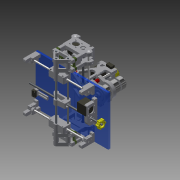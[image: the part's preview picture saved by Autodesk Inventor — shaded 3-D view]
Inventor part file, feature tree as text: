
AUTODESK INVENTOR PART (.ipt)
format: ipt  version: 2013 (Build 170138000, 138)  size: 4,507,648 bytes
history: native  units: mm
features: extrude x175, sketch x157, other x92, projected_geometry x32, fillet x19, mirror x18
ambient origin geometry x8: Origin, YZ Plane, XZ Plane, XY Plane, X Axis, Y Axis, Z Axis, Center Point
feature tree (493):
  other  "spindle.ipt"
  other  "spodnítyče"
  other  "Bloky"
  extrude  "Vysunutí1"  Depth=80.0mm
  extrude  "Vysunutí2"  Depth=4.2mm
  extrude  "Vysunutí6"  Depth=10.0mm
  extrude  "Vysunutí3"  Depth=30.0mm
  extrude  "Vysunutí4"  Depth=45.0mm
  extrude  "Vysunutí5"  Depth=300.0mm TaperAngle=0.0deg
  extrude  "Vysunutí8"  Depth=4.4mm
  extrude  "Vysunutí33"  Depth=300.0mm TaperAngle=0.0deg
  extrude  "Vysunutí9"  Depth=16.0mm
  extrude  "Vysunutí11"  Depth=100.0mm
  extrude  "Vysunutí13"  Depth=21.5mm
  extrude  "Vysunutí14"  Depth=15.0mm TaperAngle=0.0deg
  extrude  "Vysunutí15"  Depth=10.0mm TaperAngle=0.0deg
  extrude  "Vysunutí16"  Depth=15.0mm TaperAngle=0.0deg
  extrude  "Vysunutí17"  Depth=30.0mm
  extrude  "Vysunutí18"  Depth=300.0mm
  extrude  "Vysunutí20"  Depth=10.0mm
  extrude  "Vysunutí22"  Depth=250.0mm TaperAngle=0.0deg
  extrude  "Vysunutí21"  Depth=15.0mm
  extrude  "Vysunutí23"  Depth=30.0mm
  fillet  "Zaoblení1"  Radius=54.8mm
  extrude  "Vysunutí31"  Depth=110.0mm
  extrude  "Vysunutí32"  Depth=10.0mm TaperAngle=0.0deg
  extrude  "Vysunutí150"  Depth=25.0mm TaperAngle=0.0deg
  extrude  "Vysunutí44"  Depth=15.0mm TaperAngle=0.0deg
  extrude  "Vysunutí45"  Depth=80.0mm TaperAngle=0.0deg
  extrude  "Vysunutí49"  TaperAngle=0.0deg  [1 undecoded]
  extrude  "Vysunutí50"  Depth=10.0mm TaperAngle=0.0deg
  extrude  "Vysunutí51"  Depth=15.0mm TaperAngle=0.0deg
  extrude  "Vysunutí54"  Depth=15.0mm TaperAngle=0.0deg
  extrude  "Vysunutí55"  Depth=15.0mm TaperAngle=0.0deg
  extrude  "Vysunutí56"  Depth=5.0mm
  extrude  "Vysunutí57"  Depth=15.0mm TaperAngle=0.0deg
  extrude  "Vysunutí75"  Depth=15.0mm TaperAngle=0.0deg
  extrude  "Vysunutí68"  Depth=15.0mm TaperAngle=0.0deg
  extrude  "Vysunutí69"  Depth=5.0mm
  extrude  "Vysunutí65"  Depth=8.5mm
  extrude  "Vysunutí66"  Depth=11.2mm
  extrude  "Vysunutí67"  Depth=4.0mm
  fillet  "Zaoblení6"  Radius=46.0mm
  extrude  "Vysunutí71"  Depth=43.0mm
  extrude  "Vysunutí72"  Depth=37.0mm
  extrude  "Vysunutí73"  Depth=31.0mm
  extrude  "Vysunutí74"  Depth=31.0mm
  extrude  "Vysunutí76"  Depth=4.5mm
  extrude  "Vysunutí77"  Depth=80.0mm TaperAngle=0.0deg
  extrude  "Vysunutí78"  Depth=80.0mm TaperAngle=0.0deg
  sketch  "Náčrt73"
  extrude  "Vysunutí82"  Depth=7.0mm
  extrude  "Vysunutí81"  Depth=80.0mm TaperAngle=0.0deg
  extrude  "Vysunutí151"  Depth=20.0mm
  extrude  "Vysunutí228"  Depth=20.0mm
  mirror  "Zrcadlit1"
  mirror  "Zrcadlit2"
  mirror  "Zrcadlit3"
  mirror  "Zrcadlit4"
  mirror  "Zrcadlit5"
  mirror  "Zrcadlit6"
  mirror  "Zrcadlit7"
  mirror  "Zrcadlit9"
  extrude  "Vysunutí84"  Depth=5.0mm TaperAngle=0.0deg
  other  "Posunout těleso1"
  extrude  "Vysunutí85"  Depth=5.0mm TaperAngle=0.0deg
  fillet  "Zaoblení7"  Radius=15.0mm
  extrude  "Vysunutí86"  Depth=23.0mm
  extrude  "Vysunutí87"  Depth=10.0mm TaperAngle=0.0deg
  extrude  "Vysunutí88"  Depth=10.0mm TaperAngle=0.0deg
  extrude  "Vysunutí112"  Depth=23.0mm
  fillet  "Zaoblení8"  Radius=10.0mm
  mirror  "Zrcadlit10"
  mirror  "Zrcadlit11"
  mirror  "Zrcadlit12"
  extrude  "Vysunutí93"  Depth=3.0mm
  mirror  "Zrcadlit13"
  other  "Pracovní rovina26"
  extrude  "Vysunutí121"  Depth=5.0mm
  extrude  "Vysunutí136"  Depth=3.0mm
  extrude  "Vysunutí94"  Depth=3.0mm
  extrude  "Vysunutí95"  Depth=10.0mm TaperAngle=0.0deg
  extrude  "Vysunutí96"  Depth=10.0mm TaperAngle=0.0deg
  extrude  "Vysunutí97"  Depth=4.0mm
  extrude  "Vysunutí98"  Depth=10.0mm TaperAngle=0.0deg
  extrude  "Vysunutí99"  Depth=380.0mm TaperAngle=0.0deg
  extrude  "Vysunutí100"  Depth=14.0mm
  extrude  "Vysunutí101"  Depth=1.0mm
  extrude  "Vysunutí102"  Depth=10.0mm
  fillet  "Zaoblení9"  Radius=1.0mm
  fillet  "Zaoblení10"  Radius=35.0mm
  fillet  "Zaoblení11"  Radius=1.7mm
  extrude  "Vysunutí103"  Depth=14.0mm
  extrude  "Vysunutí104"  Depth=1.0mm
  other  "Pracovní rovina22"
  extrude  "Vysunutí106"  Depth=1.0mm
  other  "Pracovní rovina25"
  extrude  "Vysunutí107"  Depth=14.0mm
  extrude  "Vysunutí119"  Depth=14.0mm
  mirror  "Zrcadlit17"
  extrude  "Vysunutí124"  Depth=20.0mm
  extrude  "Vysunutí125"  Depth=3.0mm
  extrude  "Vysunutí126"  Depth=3.0mm
  extrude  "Vysunutí130"  Depth=15.0mm TaperAngle=0.0deg
  extrude  "Vysunutí127"  Depth=10.0mm TaperAngle=0.0deg
  extrude  "Vysunutí137"  Depth=10.0mm TaperAngle=0.0deg
  mirror  "Zrcadlit18"
  extrude  "Vysunutí135"  Depth=4.0mm
  other  "Kombinovat1"
  extrude  "Vysunutí143"  Depth=10.0mm TaperAngle=0.0deg
  extrude  "Vysunutí144"  Depth=10.0mm TaperAngle=0.0deg
  extrude  "Vysunutí145"  Depth=13.0mm
  extrude  "Vysunutí146"  Depth=10.0mm TaperAngle=0.0deg
  extrude  "Vysunutí147"  Depth=4.0mm
  extrude  "Vysunutí148"  Depth=6.0mm
  extrude  "Vysunutí149"  Depth=6.0mm
  extrude  "Vysunutí153"  Depth=10.0mm TaperAngle=0.0deg
  extrude  "Vysunutí154"  Depth=1.4mm
  extrude  "Vysunutí155"  Depth=1.4mm
  extrude  "Vysunutí156"  Depth=10.0mm TaperAngle=0.0deg
  extrude  "Vysunutí157"  Depth=11.2mm
  extrude  "Vysunutí158"  Depth=4.0mm TaperAngle=0.0deg
  extrude  "Vysunutí159"  Depth=15.0mm TaperAngle=0.0deg
  extrude  "Vysunutí160"  Depth=15.0mm TaperAngle=0.0deg
  extrude  "Vysunutí161"  Depth=11.2mm
  extrude  "Vysunutí162"  Depth=4.0mm TaperAngle=0.0deg
  extrude  "Vysunutí163"  Depth=0.6mm TaperAngle=0.0deg
  extrude  "Vysunutí164"  Depth=15.0mm TaperAngle=0.0deg
  extrude  "Vysunutí165"  Depth=15.0mm TaperAngle=0.0deg
  extrude  "Vysunutí166"  Depth=4.0mm
  extrude  "Vysunutí167"  Depth=300.0mm TaperAngle=0.0deg
  extrude  "Vysunutí168"  Depth=10.0mm
  extrude  "Vysunutí169"  Depth=80.0mm TaperAngle=0.0deg
  extrude  "Vysunutí170"  Depth=14.0mm
  extrude  "Vysunutí171"  Depth=15.0mm
  extrude  "Vysunutí172"  Depth=10.0mm
  extrude  "Vysunutí173"  Depth=15.0mm TaperAngle=0.0deg
  extrude  "Vysunutí174"  Depth=4.0mm
  extrude  "Vysunutí175"  Depth=1.8mm
  extrude  "Vysunutí176"  Depth=40.0mm TaperAngle=0.0deg
  extrude  "Vysunutí179"  Depth=10.0mm TaperAngle=0.0deg
  extrude  "Vysunutí180"  Depth=10.0mm TaperAngle=0.0deg
  extrude  "Vysunutí181"  Depth=2.0mm
  extrude  "Vysunutí182"  Depth=45.0mm TaperAngle=0.0deg
  extrude  "Vysunutí183"  Depth=15.0mm TaperAngle=0.0deg
  extrude  "Vysunutí184"  Depth=45.0mm
  extrude  "Vysunutí185"  Depth=10.0mm TaperAngle=0.0deg
  extrude  "Vysunutí187"  Depth=11.2mm
  extrude  "Vysunutí188"  Depth=4.0mm TaperAngle=0.0deg
  fillet  "Zaoblení12"  Radius=0.6mm
  extrude  "Vysunutí190"  Depth=30.0mm
  extrude  "Vysunutí191"  Depth=15.0mm
  extrude  "Vysunutí192"  Depth=10.0mm
  fillet  "Zaoblení13"  Radius=15.0mm
  extrude  "Vysunutí193"  Depth=10.0mm
  extrude  "Vysunutí194"  Depth=15.0mm
  extrude  "Vysunutí195"  Depth=10.0mm
  extrude  "Vysunutí196"  Depth=15.0mm
  extrude  "Vysunutí197"  Depth=15.0mm TaperAngle=0.0deg
  extrude  "Vysunutí198"  Depth=18.0mm
  extrude  "Vysunutí199"  Depth=4.0mm TaperAngle=0.0deg
  extrude  "Vysunutí200"  Depth=20.0mm
  fillet  "Zaoblení14"  Radius=20.0mm
  extrude  "Vysunutí201"  Depth=10.0mm TaperAngle=0.0deg
  extrude  "Vysunutí202"  Depth=2.5mm
  extrude  "Vysunutí203"  Depth=10.0mm TaperAngle=0.0deg
  extrude  "Vysunutí204"  Depth=20.0mm
  extrude  "Vysunutí205"  Depth=5.0mm
  fillet  "Zaoblení15"  Radius=10.0mm
  extrude  "Vysunutí206"  Depth=7.5mm
  extrude  "Vysunutí207"  Depth=10.0mm TaperAngle=0.0deg
  extrude  "Vysunutí211"  Depth=2.0mm
  extrude  "Vysunutí212"  Depth=1.0mm
  extrude  "Vysunutí213"  Depth=2.0mm TaperAngle=0.0deg
  extrude  "Vysunutí214"  Depth=5.0mm
  fillet  "Zaoblení16"  Radius=5.0mm
  extrude  "Vysunutí215"  Depth=3.0mm
  mirror  "Zrcadlit21"
  extrude  "Vysunutí216"  Depth=3.0mm
  extrude  "Vysunutí217"  Depth=3.0mm
  extrude  "Vysunutí218"  Depth=3.0mm
  fillet  "Zaoblení17"  Radius=16.0mm
  extrude  "Vysunutí220"  Depth=19.0mm
  extrude  "Vysunutí221"  Depth=5.0mm
  extrude  "Vysunutí222"  Depth=60.0mm
  extrude  "Vysunutí223"  Depth=8.1mm
  extrude  "Vysunutí224"  Depth=15.5mm
  extrude  "Vysunutí225"  Depth=50.0mm
  extrude  "Vysunutí226"  Depth=150.0mm TaperAngle=0.0deg
  extrude  "Vysunutí227"  Depth=15.3mm
  extrude  "Vysunutí229"  Depth=49.0mm TaperAngle=0.0deg
  fillet  "Zaoblení18"  Radius=15.0mm
  fillet  "Zaoblení19"  Radius=20.0mm
  extrude  "Vysunutí230"  Depth=35.0mm
  extrude  "Vysunutí231"  Depth=15.3mm
  extrude  "Vysunutí232"  Depth=24.5mm TaperAngle=0.0deg
  extrude  "Vysunutí233"  Depth=12.0mm
  extrude  "Vysunutí234"  Depth=45.0mm
  extrude  "Vysunutí235"  Depth=10.0mm
  extrude  "Vysunutí236"  Depth=15.0mm
  extrude  "Vysunutí237"  Depth=10.0mm
  extrude  "Vysunutí238"  Depth=10.0mm
  fillet  "Zaoblení20"  Radius=10.0mm
  extrude  "Vysunutí239"  Depth=10.0mm
  other  "Pracovní rovina31"
  mirror  "Zrcadlit22"
  extrude  "Vysunutí240"  Depth=10.0mm TaperAngle=0.0deg
  extrude  "Vysunutí241"  Depth=10.0mm TaperAngle=0.0deg
  extrude  "Vysunutí242"  Depth=25.0mm TaperAngle=0.0deg
  extrude  "Vysunutí243"  Depth=25.0mm TaperAngle=0.0deg
  fillet  "Zaoblení21"  Radius=25.0mm
  fillet  "Zaoblení22"  Radius=15.1mm
  mirror  "Zrcadlit23"
  mirror  "Zrcadlit24"
  other  "Závit1"
  other  "Závit2"
  other  "Závit3"
  extrude  "Vysunutí244"  Depth=25.0mm TaperAngle=0.0deg
  extrude  "Vysunutí245"  Depth=11.0mm
  extrude  "Vysunutí246"  Depth=30.0mm TaperAngle=0.0deg
  extrude  "Vysunutí247"  Depth=28.0mm
  fillet  "Zaoblení24"  Radius=30.0mm
  sketch  "Náčrt249"
  extrude  "Vysunutí248"  Depth=43.0mm
  extrude  "Vysunutí249"  Depth=47.0mm
  extrude  "Vysunutí250"  Depth=43.0mm TaperAngle=0.0deg
  sketch  "Náčrt2"
  other  "pohonY"
  sketch  "Náčrt3"
  projected_geometry  "Promítnutá smyčka1"
  projected_geometry  "Promítnutá smyčka2"
  other  "drzaky1"
  sketch  "Náčrt4"
  sketch  "Náčrt5"
  sketch  "Náčrt6"
  other  "stul"
  sketch  "Náčrt9"
  sketch  "Náčrt11"
  other  "drzaky2"
  sketch  "Náčrt14"
  other  "yvozík1"
  other  "yvozík2"
  sketch  "Náčrt18"
  projected_geometry  "Promítnutá smyčka8"
  projected_geometry  "Promítnutá smyčka9"
  sketch  "Náčrt19"
  sketch  "Náčrt20"
  sketch  "Náčrt21"
  sketch  "Náčrt23"
  sketch  "Náčrt24"
  sketch  "Náčrt25"
  sketch  "Náčrt26"
  sketch  "Náčrt27"
  sketch  "Náčrt31"
  sketch  "Náčrt33"
  sketch  "Náčrt41"
  sketch  "Náčrt44"
  sketch  "Náčrt45"
  other  "drzakxvnejsi"
  sketch  "Náčrt48"
  projected_geometry  "Promítnutá smyčka33"
  sketch  "Náčrt50"
  other  "Podložka horni"
  sketch  "Náčrt51"
  other  "posuvx"
  sketch  "Náčrt52"
  other  "tycex"
  sketch  "Náčrt53"
  sketch  "Náčrt54"
  sketch  "Náčrt56"
  sketch  "Náčrt58"
  sketch  "Náčrt60"
  other  "rozpěrka"
  sketch  "Náčrt64"
  projected_geometry  "Promítnutá smyčka40"
  sketch  "Náčrt65"
  sketch  "Náčrt67"
  other  "drzakXvnitrni"
  sketch  "Náčrt70"
  sketch  "Náčrt71"
  sketch  "Náčrt72"
  other  "Pole Podložka horni:1"
  other  "Těleso27"
  other  "Podložka"
  other  "Pole Podložka horni:2"
  other  "Těleso29"
  other  "Pole Podložka horni:3"
  other  "Těleso30"
  other  "Pole Podložka horni:4"
  other  "Těleso31"
  other  "Pole Podložka horni:5"
  other  "srzakxLnirni"
  other  "Pole Podložka horni:6"
  other  "Těleso33"
  other  "Pole Podložka horni:7"
  other  "Těleso34"
  other  "Pole Podložka horni:9"
  other  "Těleso36"
  sketch  "Náčrt77"
  other  "tyceY"
  other  "Těleso1::spindle.ipt"
  other  "Prvek štítků1"
  sketch  "Náčrt78"
  sketch  "Náčrt79"
  projected_geometry  "Promítnutá smyčka44"
  other  "NohaLZ"
  sketch  "Náčrt80"
  sketch  "Náčrt81"
  sketch  "Náčrt83"
  other  "Pole Podložka horni:10"
  other  "NohaPZ"
  other  "Pole Podložka horni:11"
  other  "NohaLP"
  other  "Pole Podložka horni:12"
  other  "NohaPP"
  sketch  "Náčrt87"
  other  "Těleso43"
  other  "Pole Podložka horni:13"
  other  "Těleso44"
  sketch  "Náčrt88"
  projected_geometry  "Promítnutá smyčka45"
  other  "drzakmotoruY"
  sketch  "Náčrt89"
  sketch  "Náčrt90"
  sketch  "Náčrt91"
  sketch  "Náčrt92"
  sketch  "Náčrt93"
  sketch  "Náčrt94"
  sketch  "Náčrt95"
  sketch  "Náčrt96"
  sketch  "Náčrt97"
  sketch  "Náčrt98"
  other  "vozikxstřed"
  sketch  "Náčrt100"
  other  "tyčeZ"
  sketch  "Náčrt101"
  other  "LM8UU2x Z"
  sketch  "Náčrt116"
  other  "lm8uu X"
  sketch  "Náčrt118"
  other  "vozikxL"
  sketch  "Náčrt119"
  other  "Pole drzakmotoruY:15"
  other  "vozíkxP"
  sketch  "Náčrt120"
  projected_geometry  "Promítnutá smyčka58"
  sketch  "Náčrt128"
  other  "Těleso64"
  sketch  "Náčrt129"
  projected_geometry  "Promítnutá smyčka61"
  sketch  "Náčrt135"
  other  "motorZ"
  sketch  "Náčrt137"
  sketch  "Náčrt138"
  sketch  "Náčrt139"
  other  "drzakmotoruZ"
  sketch  "Náčrt141"
  sketch  "Náčrt142"
  other  "drzakvretenahorní"
  projected_geometry  "Promítnutá smyčka65"
  sketch  "Náčrt144"
  projected_geometry  "Promítnutá smyčka72"
  sketch  "Náčrt145"
  projected_geometry  "Promítnutá smyčka73"
  projected_geometry  "Promítnutá smyčka74"
  projected_geometry  "Promítnutá smyčka79"
  sketch  "Náčrt146"
  other  "drzakxLvnejsi"
  sketch  "Náčrt147"
  projected_geometry  "Promítnutá smyčka83"
  projected_geometry  "Promítnutá smyčka85"
  sketch  "Náčrt148"
  sketch  "Náčrt149"
  sketch  "Náčrt150"
  projected_geometry  "Promítnutá smyčka86"
  sketch  "Náčrt151"
  sketch  "Náčrt154"
  sketch  "Náčrt155"
  sketch  "Náčrt157"
  other  "sroubZ"
  projected_geometry  "Promítnutá smyčka89"
  sketch  "Náčrt158"
  projected_geometry  "Promítnutá smyčka90"
  sketch  "Náčrt159"
  other  "drzakvretenaspodní"
  sketch  "Náčrt160"
  sketch  "Náčrt161"
  sketch  "Náčrt162"
  sketch  "Náčrt163"
  sketch  "Náčrt164"
  sketch  "Náčrt165"
  sketch  "Náčrt166"
  projected_geometry  "Promítnutá smyčka91"
  sketch  "Náčrt167"
  other  "motorX"
  sketch  "Náčrt168"
  sketch  "Náčrt169"
  sketch  "Náčrt172"
  sketch  "Náčrt173"
  projected_geometry  "Promítnutá smyčka92"
  sketch  "Náčrt174"
  sketch  "Náčrt175"
  sketch  "Náčrt176"
  sketch  "Náčrt177"
  sketch  "Náčrt178"
  other  "drzakmatkyx"
  sketch  "Náčrt180"
  sketch  "Náčrt181"
  other  "matkax"
  sketch  "Náčrt182"
  sketch  "Náčrt183"
  sketch  "Náčrt184"
  other  "matkax2"
  sketch  "Náčrt185"
  sketch  "Náčrt186"
  sketch  "Náčrt187"
  sketch  "Náčrt188"
  sketch  "Náčrt189"
  sketch  "Náčrt190"
  sketch  "Náčrt191"
  sketch  "Náčrt192"
  sketch  "Náčrt193"
  sketch  "Náčrt196"
  other  "dorazZ"
  sketch  "Náčrt197"
  sketch  "Náčrt198"
  sketch  "Náčrt201"
  other  "Těleso78"
  sketch  "Náčrt206"
  sketch  "Náčrt207"
  sketch  "Náčrt208"
  sketch  "Náčrt209"
  sketch  "Náčrt210"
  other  "Pole srzakxLnirni:16"
  other  "Těleso79"
  sketch  "Náčrt211"
  sketch  "Náčrt212"
  projected_geometry  "Promítnutá smyčka93"
  sketch  "Náčrt214"
  sketch  "Náčrt217"
  sketch  "Náčrt218"
  sketch  "Náčrt219"
  other  "Těleso80"
  sketch  "Náčrt220"
  sketch  "Náčrt221"
  other  "dorazX"
  sketch  "Náčrt222"
  sketch  "Náčrt223"
  other  "Těleso82"
  projected_geometry  "Promítnutá smyčka94"
  sketch  "Náčrt226"
  sketch  "Náčrt227"
  sketch  "Náčrt228"
  sketch  "Náčrt229"
  sketch  "Náčrt230"
  sketch  "Náčrt231"
  other  "podlozkalm8uuX"
  sketch  "Náčrt232"
  other  "Těleso84"
  sketch  "Náčrt233"
  sketch  "Náčrt234"
  other  "Těleso85"
  sketch  "Náčrt235"
  sketch  "Náčrt236"
  sketch  "Náčrt237"
  sketch  "Náčrt239"
  sketch  "Náčrt240"
  sketch  "Náčrt241"
  other  "manualniovladani"
  sketch  "Náčrt242"
  sketch  "Náčrt245"
  other  "motorY"
  sketch  "Náčrt246"
  sketch  "Náčrt247"
  sketch  "Náčrt248"
  projected_geometry  "Promítnutá smyčka95"
  projected_geometry  "Promítnutá smyčka96"
  projected_geometry  "Promítnutá smyčka97"
  projected_geometry  "Promítnutá smyčka98"
  projected_geometry  "Promítnutá smyčka99"
  projected_geometry  "Promítnutá smyčka100"
  projected_geometry  "Promítnutá smyčka101"
  projected_geometry  "Promítnutá smyčka102"
  other  "Blok1"
  sketch  "Náčrt252"
  other  "motor"
  sketch  "Náčrt253"
  sketch  "Náčrt254"
  other  "vreteno"
  other  "Blok1:1"
  other  "motor:1"
  other  "motor:2"
  other  "motor:3"
note: 1 required parameter value undecoded (feature->parameter linkage not recoverable at this tier; creation-order binding heuristic only, values carry confidence <= 0.55)
